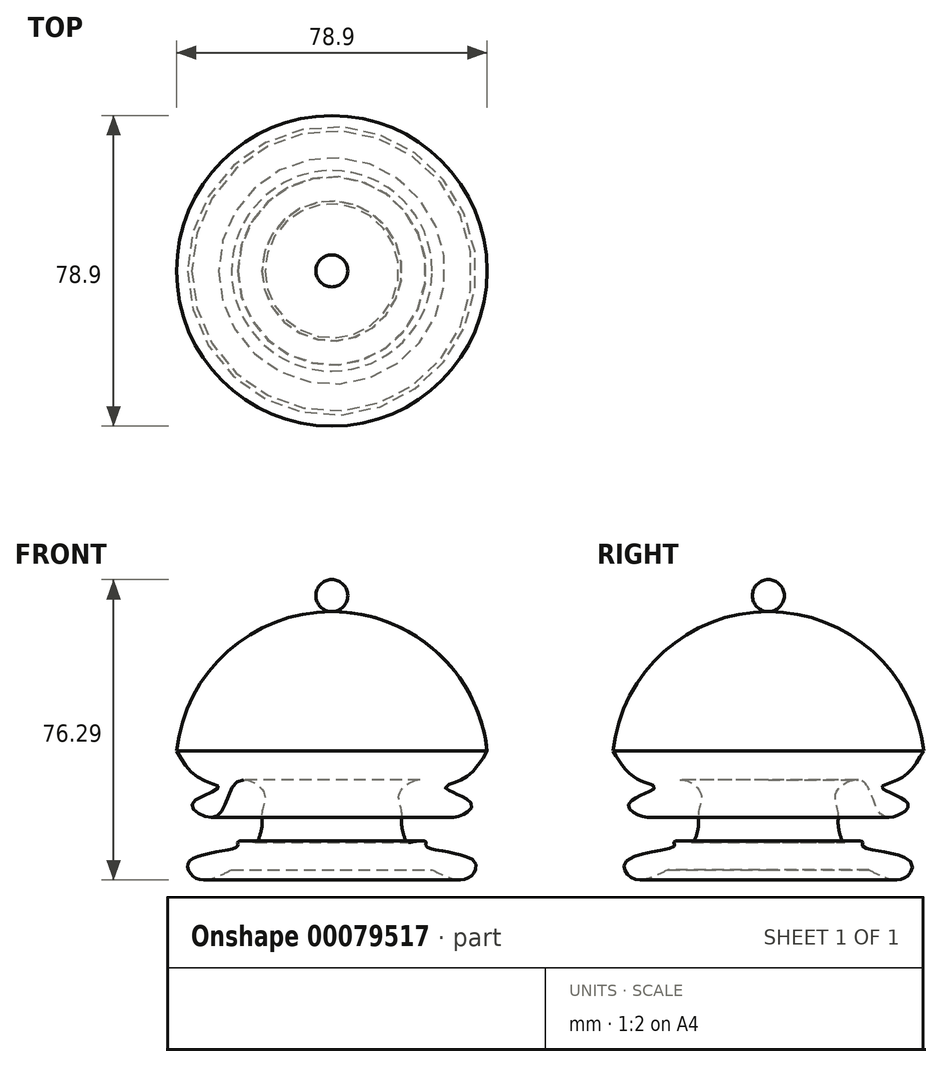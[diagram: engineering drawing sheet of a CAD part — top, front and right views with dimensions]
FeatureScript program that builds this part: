
annotation { "Feature Type Name" : "Feature", "Feature Type Description" : "" }
export const myFeature = defineFeature(function(context is Context, id is Id, definition is map)
    precondition{}
    {
        {
            var Q0;
            Q0=qCreatedBy(makeId("Front.planeOp"),FACE);
            var sketch = newSketch(context, id + "F0", { "sketchPlane" : qUnion([Q0])});
            skLineSegment(sketch, "E0", {"start": v(0, 0) * mm, "end": v(0, 73.72) * mm});
            skArc(sketch, "E1", {"start": v(4.06, 69.66) * mm, "mid": v(2.87, 72.53) * mm, "end": v(0, 73.72) * mm});
            skArc(sketch, "E2", {"start": v(0, 65.6) * mm, "mid": v(2.87, 66.8) * mm, "end": v(4.06, 69.66) * mm});
            skArc(sketch, "E3", {"start": v(39.45, 30.14) * mm, "mid": v(26.52, 55.44) * mm, "end": v(0, 65.6) * mm});
            skFitSpline(sketch, "E4", {"points": [v(39.45, 30.14) * mm, v(33.25, 23.05) * mm, v(28.81, 20.83) * mm, v(35.46, 16.84) * mm, v(32.58, 13.74) * mm, v(28.15, 14.63) * mm, v(23.71, 22.6) * mm, v(17.29, 19.73) * mm, v(17.73, 14.85) * mm, v(17.73, 11.52) * mm, v(19.06, 7.1) * mm, v(20.4, 7.1) * mm, v(23.94, 7.1) * mm, v(23.94, 5.98) * mm, v(36.13, 2.22) * mm, v(34.35, -2.22) * mm, v(25.49, 0) * mm], "startDerivative": vector(-60.17, -101.2) * mm, "endDerivative": vector(-118.4, 60.73) * mm});
            skLineSegment(sketch, "E5", {"start": v(0, 0) * mm, "end": v(25.49, 0) * mm});
            skSolve(sketch);
        }
        {
            var Q0;
            {var subQ2=sQuery(id+"F0.wireOp",EDGE,"E3");Q0=makeQuery(id+"F0.imprint","IMPRINT",FACE,{"disambiguationData":[TD([[makeQuery(id+"F0.imprint","IMPRINT",EDGE,{"derivedFrom":subQ2}),1.0]])]});}
            var Q1;
            {var subQ0=sQuery(id+"F0.wireOp",EDGE,"E1");Q1=makeQuery(id+"F0.imprint","IMPRINT",FACE,{"disambiguationData":[TD([[makeQuery(id+"F0.imprint","IMPRINT",EDGE,{"derivedFrom":subQ0}),1.0]])]});}
            var Q2;
            Q2=sQuery(id+"F0.wireOp",EDGE,"E0");
            revolve(context, id + "F1", {"entities" : qUnion([Q0, Q1]), "axis" : qUnion([Q2]), "revolveType" : RevolveType.FULL});
        }
    });
